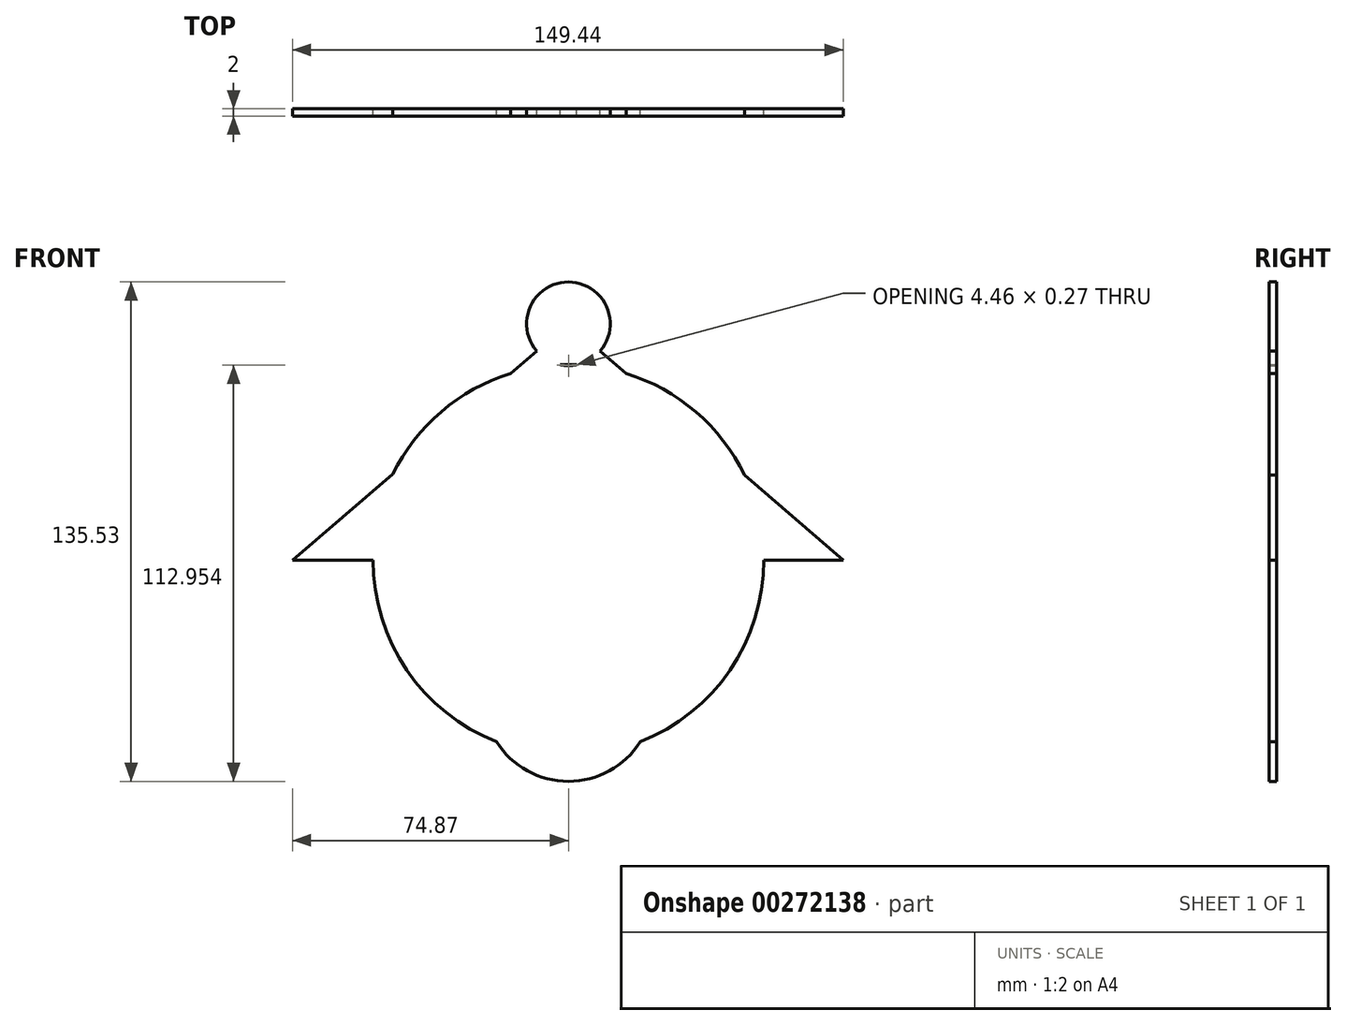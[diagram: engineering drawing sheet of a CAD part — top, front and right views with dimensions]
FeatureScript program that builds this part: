
annotation { "Feature Type Name" : "Feature", "Feature Type Description" : "" }
export const myFeature = defineFeature(function(context is Context, id is Id, definition is map)
    precondition{}
    {
        {
            var Q0;
            Q0=qCreatedBy(makeId("Front.planeOp"),FACE);
            var sketch = newSketch(context, id + "F0", { "sketchPlane" : qUnion([Q0])});
            skCircle(sketch, "E0", {"center": v(0, 0) * mm, "radius": 53.05 * mm});
            skCircle(sketch, "E1", {"center": v(0, -36.99) * mm, "radius": 23.05 * mm});
            skLineSegment(sketch, "E2", {"start": v(0, 64.13) * mm, "end": v(-74.87, 0) * mm});
            skLineSegment(sketch, "E3", {"start": v(-74.87, 0) * mm, "end": v(74.57, 0) * mm});
            skLineSegment(sketch, "E4", {"start": v(74.57, 0) * mm, "end": v(0, 64.13) * mm});
            skCircle(sketch, "E5", {"center": v(0, 64.13) * mm, "radius": 11.35 * mm});
            skFitSpline(sketch, "E6", {"points": [v(30.38, -43.49) * mm, v(42.66, -53.4) * mm, v(51.6, -71.3) * mm, v(52.2, -76.07) * mm], "startDerivative": vector(34.29, -20.71) * mm, "endDerivative": vector(0.13, -18.88) * mm});
            skSolve(sketch);
        }
        {
            var Q0;
            Q0 = qSketchRegion(id + "F0", true);
            var Q1;
            {var subQ0=sQuery(id+"F0.wireOp",EDGE,"4e2c3ac4-976d-4f82-9a3a-a52a4d80fa31");var subQ1=sQuery(id+"F0.wireOp",EDGE,"85EhukA6-DwI7-8EB7-bvqV-ir7a0DGDT39e");var subQ2=makeQuery(id+"F0.imprint","INTERSECT",VERTEX,{"disambiguationData":[OD(0.0)],"derivedFrom":[subQ1,subQ0]});Q1=makeQuery(id+"F0.imprint","IMPRINT",FACE,{"disambiguationData":[TD([[makeQuery(id+"F0.imprint","IMPRINT",EDGE,{"disambiguationData":[TD([[subQ2,1.0]])],"derivedFrom":subQ1}),1.0]])]});}
            var Q2;
            {var subQ0=sQuery(id+"F0.wireOp",EDGE,"4RGy97V2-RFf7-jstz-Abyh-L2aiLKpFwiGQ");Q2=makeQuery(id+"F0.imprint","IMPRINT",FACE,{"disambiguationData":[TD([[makeQuery(id+"F0.imprint","IMPRINT",EDGE,{"derivedFrom":subQ0}),-1.0]])]});}
            var Q3;
            {var subQ0=sQuery(id+"F0.wireOp",EDGE,"4e2c3ac4-976d-4f82-9a3a-a52a4d80fa31");var subQ1=sQuery(id+"F0.wireOp",EDGE,"85EhukA6-DwI7-8EB7-bvqV-ir7a0DGDT39e");var subQ2=makeQuery(id+"F0.imprint","INTERSECT",VERTEX,{"disambiguationData":[OD(0.0)],"derivedFrom":[subQ1,subQ0]});Q3=makeQuery(id+"F0.imprint","IMPRINT",FACE,{"disambiguationData":[TD([[makeQuery(id+"F0.imprint","IMPRINT",EDGE,{"disambiguationData":[TD([[subQ2,-1.0]])],"derivedFrom":subQ1}),1.0]])]});}
            var Q4;
            {var subQ0=sQuery(id+"F0.wireOp",EDGE,"rhZagDTS-SgWI-UyXs-ae8y-Dfrg1DQEBRDN");var subQ1=sQuery(id+"F0.wireOp",EDGE,"d99d93d4-4c32-4503-bbfa-80e6bcac5793.1");var subQ2=makeQuery(id+"F0.imprint","INTERSECT",VERTEX,{"disambiguationData":[OD(0.0)],"derivedFrom":[subQ1,subQ0]});Q4=makeQuery(id+"F0.imprint","IMPRINT",FACE,{"disambiguationData":[TD([[makeQuery(id+"F0.imprint","IMPRINT",EDGE,{"disambiguationData":[TD([[subQ2,-1.0]])],"derivedFrom":subQ1}),1.0]])]});}
            var Q5;
            {var subQ0=sQuery(id+"F0.wireOp",EDGE,"rhZagDTS-SgWI-UyXs-ae8y-Dfrg1DQEBRDN");var subQ1=sQuery(id+"F0.wireOp",EDGE,"d99d93d4-4c32-4503-bbfa-80e6bcac5793.0");var subQ2=makeQuery(id+"F0.imprint","INTERSECT",VERTEX,{"disambiguationData":[OD(0.0)],"derivedFrom":[subQ1,subQ0]});Q5=makeQuery(id+"F0.imprint","IMPRINT",FACE,{"disambiguationData":[TD([[makeQuery(id+"F0.imprint","IMPRINT",EDGE,{"disambiguationData":[TD([[subQ2,-1.0]])],"derivedFrom":subQ1}),1.0]])]});}
            var Q6;
            {var subQ0=sQuery(id+"F0.wireOp",EDGE,"rhZagDTS-SgWI-UyXs-ae8y-Dfrg1DQEBRDN");var subQ1=sQuery(id+"F0.wireOp",EDGE,"d99d93d4-4c32-4503-bbfa-80e6bcac5793.2");var subQ2=makeQuery(id+"F0.imprint","INTERSECT",VERTEX,{"disambiguationData":[OD(0.0)],"derivedFrom":[subQ1,subQ0]});Q6=makeQuery(id+"F0.imprint","IMPRINT",FACE,{"disambiguationData":[TD([[makeQuery(id+"F0.imprint","IMPRINT",EDGE,{"disambiguationData":[TD([[subQ2,-1.0]])],"derivedFrom":subQ1}),1.0]])]});}
            var Q7;
            {var subQ0=sQuery(id+"F0.wireOp",EDGE,"a263b3cf-b392-4a55-930c-792bdd1bc948");var subQ1=sQuery(id+"F0.wireOp",EDGE,"85EhukA6-DwI7-8EB7-bvqV-ir7a0DGDT39e");var subQ2=makeQuery(id+"F0.imprint","INTERSECT",VERTEX,{"disambiguationData":[OD(0.0)],"derivedFrom":[subQ1,subQ0]});Q7=makeQuery(id+"F0.imprint","IMPRINT",FACE,{"disambiguationData":[TD([[makeQuery(id+"F0.imprint","IMPRINT",EDGE,{"disambiguationData":[TD([[subQ2,1.0]])],"derivedFrom":subQ1}),-1.0]])]});}
            var Q8;
            {var subQ0=sQuery(id+"F0.wireOp",EDGE,"AIw4DEhh-IcG0-ei16-vj6d-3QmvjJA7jbHx");var subQ1=sQuery(id+"F0.wireOp",EDGE,"85EhukA6-DwI7-8EB7-bvqV-ir7a0DGDT39e");var subQ2=makeQuery(id+"F0.imprint","INTERSECT",VERTEX,{"disambiguationData":[OD(0.0)],"derivedFrom":[subQ1,subQ0]});Q8=makeQuery(id+"F0.imprint","IMPRINT",FACE,{"disambiguationData":[TD([[makeQuery(id+"F0.imprint","IMPRINT",EDGE,{"disambiguationData":[TD([[subQ2,1.0]])],"derivedFrom":subQ1}),1.0]])]});}
            var Q9;
            {var subQ0=sQuery(id+"F0.wireOp",EDGE,"AIw4DEhh-IcG0-ei16-vj6d-3QmvjJA7jbHx");var subQ1=sQuery(id+"F0.wireOp",EDGE,"85EhukA6-DwI7-8EB7-bvqV-ir7a0DGDT39e");var subQ2=makeQuery(id+"F0.imprint","INTERSECT",VERTEX,{"disambiguationData":[OD(0.0)],"derivedFrom":[subQ1,subQ0]});Q9=makeQuery(id+"F0.imprint","IMPRINT",FACE,{"disambiguationData":[TD([[makeQuery(id+"F0.imprint","IMPRINT",EDGE,{"disambiguationData":[TD([[subQ2,1.0]])],"derivedFrom":subQ1}),-1.0]])]});}
            var Q10;
            {var subQ0=sQuery(id+"F0.wireOp",EDGE,"AIw4DEhh-IcG0-ei16-vj6d-3QmvjJA7jbHx");var subQ1=sQuery(id+"F0.wireOp",EDGE,"85EhukA6-DwI7-8EB7-bvqV-ir7a0DGDT39e");var subQ2=makeQuery(id+"F0.imprint","INTERSECT",VERTEX,{"disambiguationData":[OD(1.0)],"derivedFrom":[subQ1,subQ0]});Q10=makeQuery(id+"F0.imprint","IMPRINT",FACE,{"disambiguationData":[TD([[makeQuery(id+"F0.imprint","IMPRINT",EDGE,{"disambiguationData":[TD([[subQ2,-1.0]])],"derivedFrom":subQ1}),-1.0]])]});}
            extrude(context, id + "F1", {"entities" : qUnion([Q0, Q1, Q2, Q3, Q4, Q5, Q6, Q7, Q8, Q9, Q10]), "depth" : 2 * mm});
        }
    });
